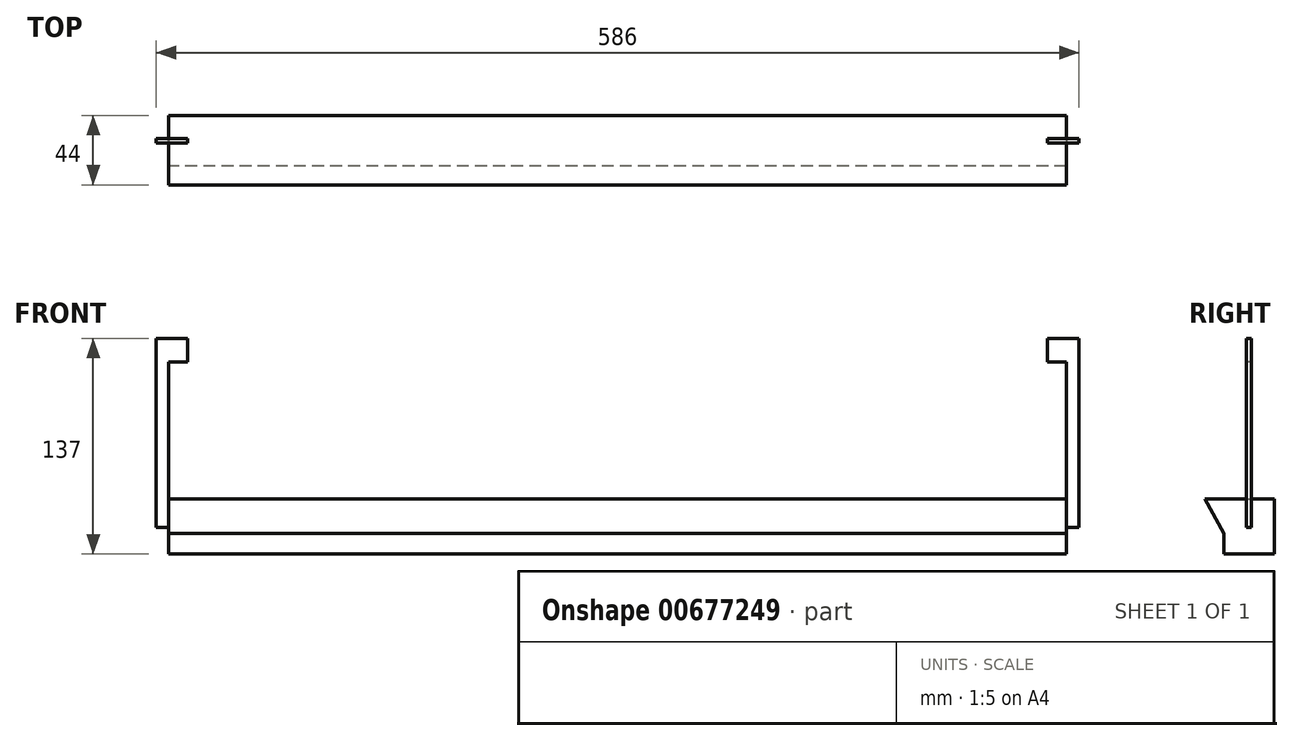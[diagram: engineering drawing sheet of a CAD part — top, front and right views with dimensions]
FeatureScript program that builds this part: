
annotation { "Feature Type Name" : "Feature", "Feature Type Description" : "" }
export const myFeature = defineFeature(function(context is Context, id is Id, definition is map)
    precondition{}
    {
        {
            var Q0;
            Q0=qCreatedBy(makeId("Top.planeOp"),FACE);
            var sketch = newSketch(context, id + "F0", { "sketchPlane" : qUnion([Q0])});
            skLineSegment(sketch, "E0.bottom", {"start": v(285, 16) * mm, "end": v(-285, 16) * mm});
            skLineSegment(sketch, "E0.top", {"start": v(285, -16) * mm, "end": v(-285, -16) * mm});
            skLineSegment(sketch, "E0.left", {"start": v(285, 16) * mm, "end": v(285, -16) * mm});
            skLineSegment(sketch, "E0.right", {"start": v(-285, 16) * mm, "end": v(-285, -16) * mm});
            skPoint(sketch, "E0.middle", {"position": v(0, 0) * mm});
            skSolve(sketch);
        }
        {
            var Q0;
            Q0=makeQuery(id+"F0.imprint","IMPRINT",FACE,{"disambiguationData":[TD([[makeQuery(id+"F0.imprint","IMPRINT",EDGE,{"derivedFrom":sQuery(id+"F0.wireOp",EDGE,"E0.bottom")}),1.0]])]});
            extrude(context, id + "F1", {"entities" : qUnion([Q0]), "depth" : 13 * mm, "offsetDistance" : 25 * mm});
        }
        {
            var Q0;
            Q0=makeQuery(id+"F1.opExtrude","SWEPT_FACE",FACE,{"disambiguationData":[OSD([sQuery(id+"F0.wireOp",EDGE,"E0.right")])]});
            var sketch = newSketch(context, id + "F2", { "sketchPlane" : qUnion([Q0])});
            skLineSegment(sketch, "E1", {"start": v(16, 13) * mm, "end": v(28, 35) * mm});
            skLineSegment(sketch, "E2", {"start": v(28, 35) * mm, "end": v(-16, 35) * mm});
            skLineSegment(sketch, "E3", {"start": v(-16, 35) * mm, "end": v(-16, 13) * mm});
            skLineSegment(sketch, "E4", {"start": v(-16, 13) * mm, "end": v(16, 13) * mm});
            skSolve(sketch);
        }
        {
            var Q0;
            Q0=makeQuery(id+"F2.imprint","IMPRINT",FACE,{"disambiguationData":[TD([[makeQuery(id+"F2.imprint","IMPRINT",EDGE,{"derivedFrom":sQuery(id+"F2.wireOp",EDGE,"E1")}),1.0]])]});
            extrude(context, id + "F3", {"entities" : qUnion([Q0]), "operationType" : NewBodyOperationType.ADD, "oppositeDirection" : true, "depth" : 570 * mm, "offsetDistance" : 25 * mm});
        }
        {
            var Q0;
            Q0=makeQuery(id+"F3.boolean.opBoolean","MERGE",FACE,{"derivedFrom":[makeQuery(id+"F1.opExtrude","SWEPT_FACE",FACE,{"disambiguationData":[OSD([sQuery(id+"F0.wireOp",EDGE,"E0.right")])]}),makeQuery(id+"F3.opExtrude","CAP_FACE",FACE,{"disambiguationData":[OSD([sQuery(id+"F2.wireOp",EDGE,"E1"),sQuery(id+"F2.wireOp",EDGE,"E2"),sQuery(id+"F2.wireOp",EDGE,"E3"),sQuery(id+"F2.wireOp",EDGE,"E4")])],"isStart":true})]});
            var sketch = newSketch(context, id + "F4", { "sketchPlane" : qUnion([Q0])});
            skLineSegment(sketch, "E5.bottom", {"start": v(1.5, 35) * mm, "end": v(-1.5, 35) * mm});
            skLineSegment(sketch, "E5.top", {"start": v(1.5, 17) * mm, "end": v(-1.5, 17) * mm});
            skLineSegment(sketch, "E5.left", {"start": v(1.5, 35) * mm, "end": v(1.5, 17) * mm});
            skLineSegment(sketch, "E5.right", {"start": v(-1.5, 35) * mm, "end": v(-1.5, 17) * mm});
            skPoint(sketch, "E5.middle", {"position": v(0, 26) * mm});
            skSolve(sketch);
        }
        {
            var Q0;
            Q0=makeQuery(id+"F4.imprint","IMPRINT",FACE,{"disambiguationData":[TD([[makeQuery(id+"F4.imprint","IMPRINT",EDGE,{"derivedFrom":sQuery(id+"F4.wireOp",EDGE,"E5.bottom")}),1.0]])]});
            extrude(context, id + "F5", {"entities" : qUnion([Q0]), "operationType" : NewBodyOperationType.ADD, "depth" : 8 * mm, "offsetDistance" : 25 * mm});
        }
        {
            var Q0;
            Q0=makeQuery(id+"F5.boolean.opBoolean","MERGE",FACE,{"derivedFrom":[makeQuery(id+"F3.opExtrude","SWEPT_FACE",FACE,{"disambiguationData":[OSD([sQuery(id+"F2.wireOp",EDGE,"E2")])]}),makeQuery(id+"F5.opExtrude","SWEPT_FACE",FACE,{"disambiguationData":[OSD([sQuery(id+"F4.wireOp",EDGE,"E5.bottom")])]})]});
            var sketch = newSketch(context, id + "F6", { "sketchPlane" : qUnion([Q0])});
            skLineSegment(sketch, "E6.bottom", {"start": v(-293, -1.5) * mm, "end": v(-285, -1.5) * mm});
            skLineSegment(sketch, "E6.top", {"start": v(-293, 1.5) * mm, "end": v(-285, 1.5) * mm});
            skLineSegment(sketch, "E6.left", {"start": v(-293, -1.5) * mm, "end": v(-293, 1.5) * mm});
            skLineSegment(sketch, "E6.right", {"start": v(-285, -1.5) * mm, "end": v(-285, 1.5) * mm});
            skSolve(sketch);
        }
        {
            var Q0;
            Q0=makeQuery(id+"F6.imprint","IMPRINT",FACE,{"disambiguationData":[TD([[makeQuery(id+"F6.imprint","IMPRINT",EDGE,{"derivedFrom":sQuery(id+"F6.wireOp",EDGE,"E6.bottom")}),1.0]])]});
            extrude(context, id + "F7", {"entities" : qUnion([Q0]), "operationType" : NewBodyOperationType.ADD, "depth" : 102 * mm, "offsetDistance" : 25 * mm});
        }
        {
            var Q0;
            Q0=makeQuery(id+"F7.opExtrude","SWEPT_FACE",FACE,{"disambiguationData":[OSD([sQuery(id+"F6.wireOp",EDGE,"E6.right")])]});
            var sketch = newSketch(context, id + "F8", { "sketchPlane" : qUnion([Q0])});
            skLineSegment(sketch, "E7.bottom", {"start": v(1.5, 137) * mm, "end": v(-1.5, 137) * mm});
            skLineSegment(sketch, "E7.top", {"start": v(1.5, 122) * mm, "end": v(-1.5, 122) * mm});
            skLineSegment(sketch, "E7.left", {"start": v(1.5, 137) * mm, "end": v(1.5, 122) * mm});
            skLineSegment(sketch, "E7.right", {"start": v(-1.5, 137) * mm, "end": v(-1.5, 122) * mm});
            skSolve(sketch);
        }
        {
            var Q0;
            Q0=makeQuery(id+"F8.imprint","IMPRINT",FACE,{"disambiguationData":[TD([[makeQuery(id+"F8.imprint","IMPRINT",EDGE,{"derivedFrom":sQuery(id+"F8.wireOp",EDGE,"E7.bottom")}),-1.0]])]});
            extrude(context, id + "F9", {"entities" : qUnion([Q0]), "operationType" : NewBodyOperationType.ADD, "depth" : 12 * mm, "offsetDistance" : 25 * mm});
        }
        {
            var Q0;
            Q0=makeQuery(id+"F3.boolean.opBoolean","MERGE",FACE,{"derivedFrom":[makeQuery(id+"F1.opExtrude","SWEPT_FACE",FACE,{"disambiguationData":[OSD([sQuery(id+"F0.wireOp",EDGE,"E0.left")])]}),makeQuery(id+"F3.opExtrude","CAP_FACE",FACE,{"disambiguationData":[OSD([sQuery(id+"F2.wireOp",EDGE,"E1"),sQuery(id+"F2.wireOp",EDGE,"E2"),sQuery(id+"F2.wireOp",EDGE,"E3"),sQuery(id+"F2.wireOp",EDGE,"E4")])],"isStart":false})]});
            var sketch = newSketch(context, id + "F10", { "sketchPlane" : qUnion([Q0])});
            skLineSegment(sketch, "E8.bottom", {"start": v(1.5, 35) * mm, "end": v(-1.5, 35) * mm});
            skLineSegment(sketch, "E8.top", {"start": v(1.5, 17) * mm, "end": v(-1.5, 17) * mm});
            skLineSegment(sketch, "E8.left", {"start": v(1.5, 35) * mm, "end": v(1.5, 17) * mm});
            skLineSegment(sketch, "E8.right", {"start": v(-1.5, 35) * mm, "end": v(-1.5, 17) * mm});
            skPoint(sketch, "E8.middle", {"position": v(0, 26) * mm});
            skPoint(sketch, "E8.middle.positionSnap0", {"position": v(0, 0) * mm});
            skPoint(sketch, "E8.centerSnap0", {"position": v(0, 0) * mm});
            skLineSegment(sketch, "E9.top", {"start": v(1.5, 137) * mm, "end": v(-1.5, 137) * mm});
            skLineSegment(sketch, "E9.left", {"start": v(1.5, 35) * mm, "end": v(1.5, 137) * mm});
            skLineSegment(sketch, "E9.right", {"start": v(-1.5, 35) * mm, "end": v(-1.5, 137) * mm});
            skSolve(sketch);
        }
        {
            var Q0;
            Q0=makeQuery(id+"F10.imprint","IMPRINT",FACE,{"disambiguationData":[TD([[makeQuery(id+"F10.imprint","IMPRINT",EDGE,{"derivedFrom":sQuery(id+"F10.wireOp",EDGE,"E8.bottom")}),1.0]])]});
            var Q1;
            Q1=makeQuery(id+"F10.imprint","IMPRINT",FACE,{"disambiguationData":[TD([[makeQuery(id+"F10.imprint","IMPRINT",EDGE,{"derivedFrom":sQuery(id+"F10.wireOp",EDGE,"E8.top")}),-1.0]])]});
            extrude(context, id + "F11", {"entities" : qUnion([Q0, Q1]), "operationType" : NewBodyOperationType.ADD, "depth" : 8 * mm, "offsetDistance" : 25 * mm});
        }
        {
            var Q0;
            Q0=makeQuery(id+"F11.opExtrude","CAP_FACE",FACE,{"disambiguationData":[OSD([sQuery(id+"F10.wireOp",EDGE,"E8.top"),sQuery(id+"F10.wireOp",EDGE,"E8.left"),sQuery(id+"F10.wireOp",EDGE,"E8.right"),sQuery(id+"F10.wireOp",EDGE,"E9.top"),sQuery(id+"F10.wireOp",EDGE,"E9.left"),sQuery(id+"F10.wireOp",EDGE,"E9.right")])],"isStart":true});
            var sketch = newSketch(context, id + "F12", { "sketchPlane" : qUnion([Q0])});
            skLineSegment(sketch, "E10.bottom", {"start": v(1.5, 137) * mm, "end": v(-1.5, 137) * mm});
            skLineSegment(sketch, "E10.top", {"start": v(1.5, 122) * mm, "end": v(-1.5, 122) * mm});
            skLineSegment(sketch, "E10.left", {"start": v(1.5, 137) * mm, "end": v(1.5, 122) * mm});
            skLineSegment(sketch, "E10.right", {"start": v(-1.5, 137) * mm, "end": v(-1.5, 122) * mm});
            skSolve(sketch);
        }
        {
            var Q0;
            Q0=makeQuery(id+"F12.imprint","IMPRINT",FACE,{"disambiguationData":[TD([[makeQuery(id+"F12.imprint","IMPRINT",EDGE,{"derivedFrom":sQuery(id+"F12.wireOp",EDGE,"E10.bottom")}),-1.0]])]});
            extrude(context, id + "F13", {"entities" : qUnion([Q0]), "operationType" : NewBodyOperationType.ADD, "depth" : 12 * mm, "offsetDistance" : 25 * mm});
        }
    });
